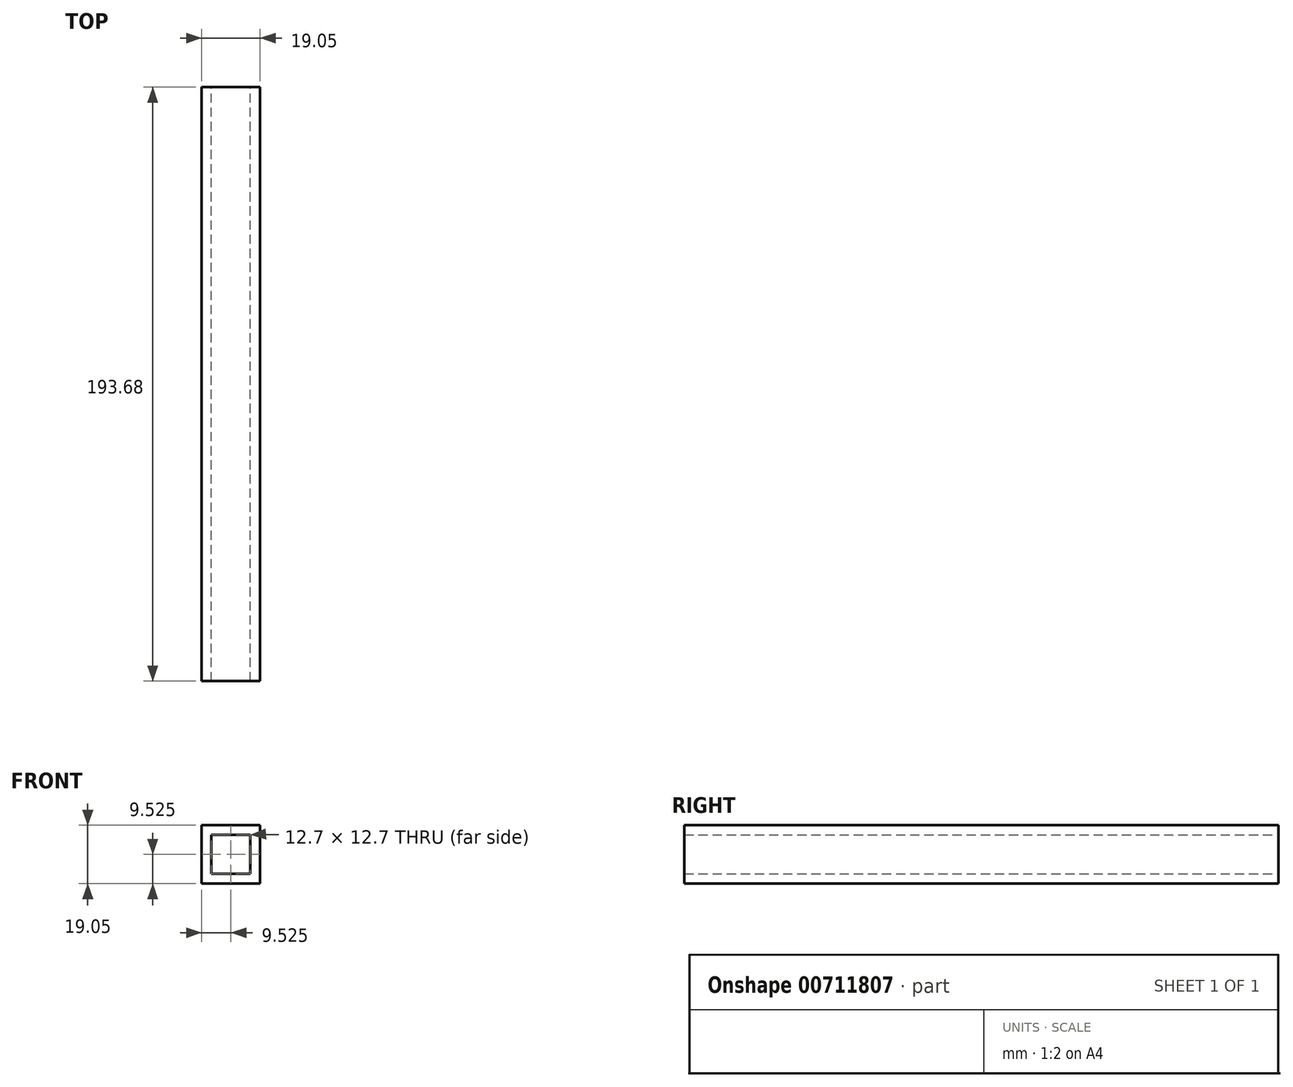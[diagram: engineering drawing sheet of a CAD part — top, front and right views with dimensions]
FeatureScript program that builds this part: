
annotation { "Feature Type Name" : "Feature", "Feature Type Description" : "" }
export const myFeature = defineFeature(function(context is Context, id is Id, definition is map)
    precondition{}
    {
        {
            var Q0;
            Q0=qCreatedBy(makeId("Front.planeOp"),FACE);
            var sketch = newSketch(context, id + "F0", { "sketchPlane" : qUnion([Q0])});
            skLineSegment(sketch, "E0.bottom", {"start": v(0, 0) * mm, "end": v(19.05, 0) * mm});
            skLineSegment(sketch, "E0.top", {"start": v(0, 19.05) * mm, "end": v(19.05, 19.05) * mm});
            skLineSegment(sketch, "E0.left", {"start": v(0, 0) * mm, "end": v(0, 19.05) * mm});
            skLineSegment(sketch, "E0.right", {"start": v(19.05, 0) * mm, "end": v(19.05, 19.05) * mm});
            skLineSegment(sketch, "E1.bottom", {"start": v(3.17, 3.18) * mm, "end": v(15.88, 3.18) * mm});
            skLineSegment(sketch, "E1.top", {"start": v(3.17, 15.88) * mm, "end": v(15.88, 15.88) * mm});
            skLineSegment(sketch, "E1.left", {"start": v(3.17, 3.18) * mm, "end": v(3.17, 15.88) * mm});
            skLineSegment(sketch, "E1.right", {"start": v(15.88, 3.18) * mm, "end": v(15.88, 15.88) * mm});
            skSolve(sketch);
        }
        {
            var Q0;
            Q0 = qSketchRegion(id + "F0", true);
            extrude(context, id + "F1", {"entities" : qUnion([Q0]), "depth" : 193.67 * mm, "offsetDistance" : 25.4 * mm});
        }
    });
